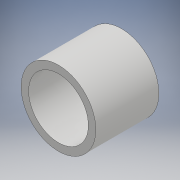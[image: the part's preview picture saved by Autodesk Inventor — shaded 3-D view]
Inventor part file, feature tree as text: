
AUTODESK INVENTOR PART (.ipt)
format: ipt  version: 2018 (Build 220112000, 112)  size: 99,840 bytes
history: native  units: mm
features: extrude x1, sketch x1
ambient origin geometry x8: Origin, YZ Plane, XZ Plane, XY Plane, X Axis, Y Axis, Z Axis, Center Point
bodies: Solid1 (feature_tree)
feature tree (2):
  extrude  "Extrusion1"  Depth=6.75mm
  sketch  "Sketch1"  dims[d0=6.4mm d1=8.0mm d2=6.75mm d3=0.0mm]
